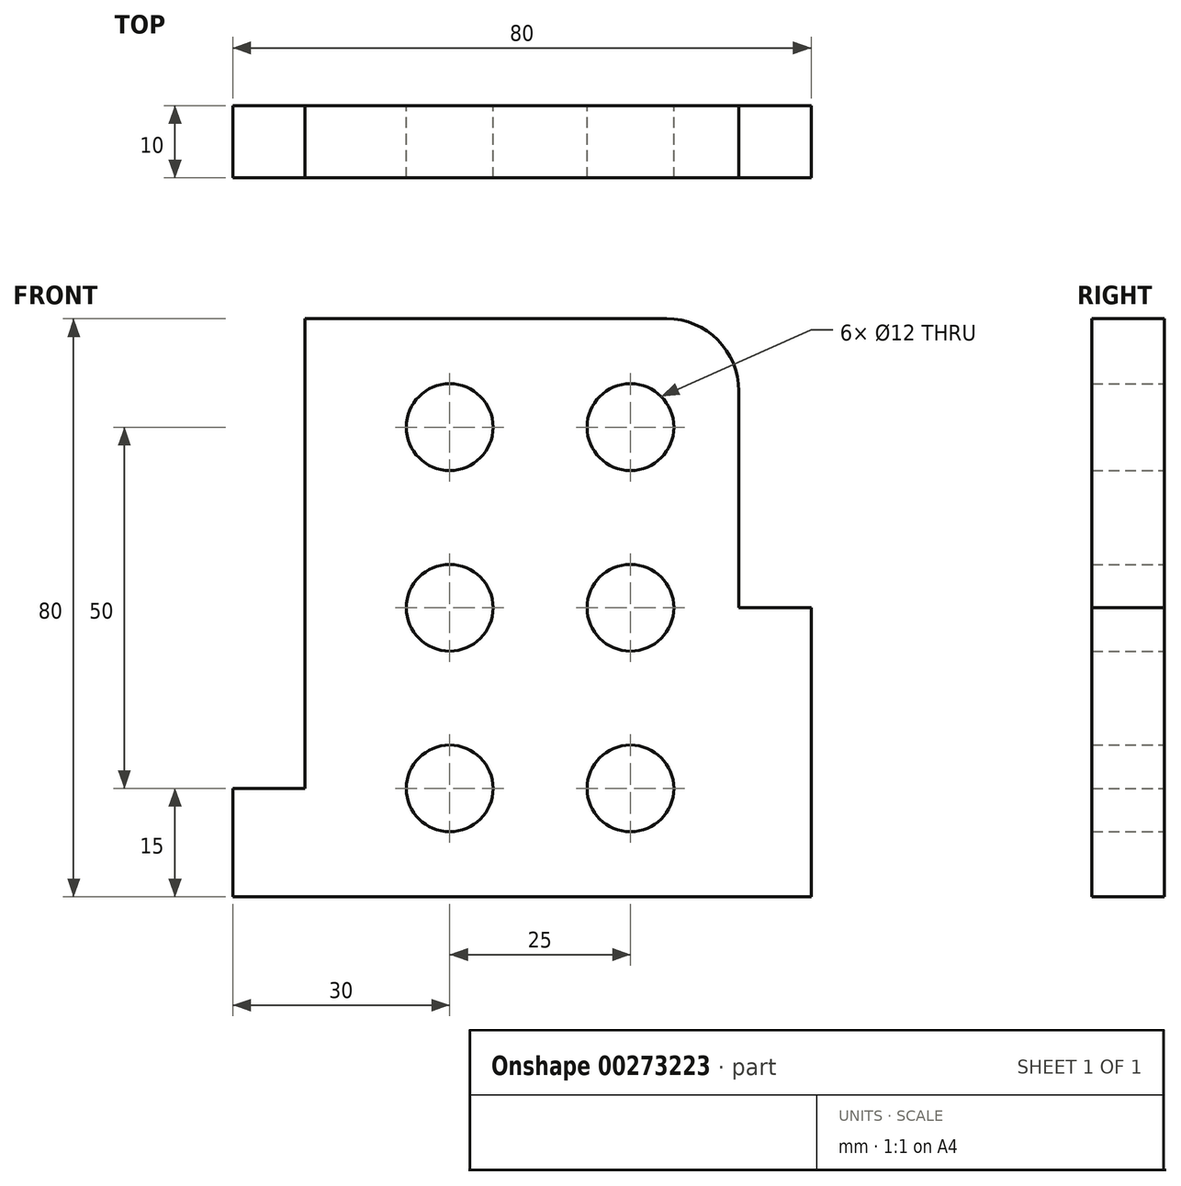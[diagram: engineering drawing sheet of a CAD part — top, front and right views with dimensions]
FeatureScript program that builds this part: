
annotation { "Feature Type Name" : "Feature", "Feature Type Description" : "" }
export const myFeature = defineFeature(function(context is Context, id is Id, definition is map)
    precondition{}
    {
        {
            var Q0;
            Q0=qCreatedBy(makeId("Front.planeOp"),FACE);
            var sketch = newSketch(context, id + "F0", { "sketchPlane" : qUnion([Q0])});
            skLineSegment(sketch, "E0", {"start": v(0, 0) * mm, "end": v(80, 0) * mm});
            skLineSegment(sketch, "E1", {"start": v(80, 0) * mm, "end": v(80, 40) * mm});
            skLineSegment(sketch, "E2", {"start": v(0, 0) * mm, "end": v(0, 15) * mm});
            skCircle(sketch, "E3", {"center": v(30, 65) * mm, "radius": 6 * mm});
            skCircle(sketch, "E4", {"center": v(55, 65) * mm, "radius": 6 * mm});
            skCircle(sketch, "E5", {"center": v(55, 40) * mm, "radius": 6 * mm});
            skCircle(sketch, "E6", {"center": v(30, 15) * mm, "radius": 6 * mm});
            skCircle(sketch, "E7", {"center": v(55, 15) * mm, "radius": 6 * mm});
            skLineSegment(sketch, "E8", {"start": v(0, 15) * mm, "end": v(10, 15) * mm});
            skLineSegment(sketch, "E9", {"start": v(10, 15) * mm, "end": v(10, 80) * mm});
            skLineSegment(sketch, "E10", {"start": v(10, 80) * mm, "end": v(60, 80) * mm});
            skLineSegment(sketch, "E11", {"start": v(80, 40) * mm, "end": v(70, 40) * mm});
            skLineSegment(sketch, "E12", {"start": v(70, 40) * mm, "end": v(70, 70) * mm});
            skCircle(sketch, "E13", {"center": v(30, 40) * mm, "radius": 6 * mm});
            skArc(sketch, "E14", {"start": v(60, 80) * mm, "mid": v(67.07, 77.07) * mm, "end": v(70, 70) * mm});
            skSolve(sketch);
        }
        {
            var Q0;
            Q0 = qSketchRegion(id + "F0", true);
            extrude(context, id + "F1", {"entities" : qUnion([Q0]), "depth" : 10 * mm});
        }
    });
